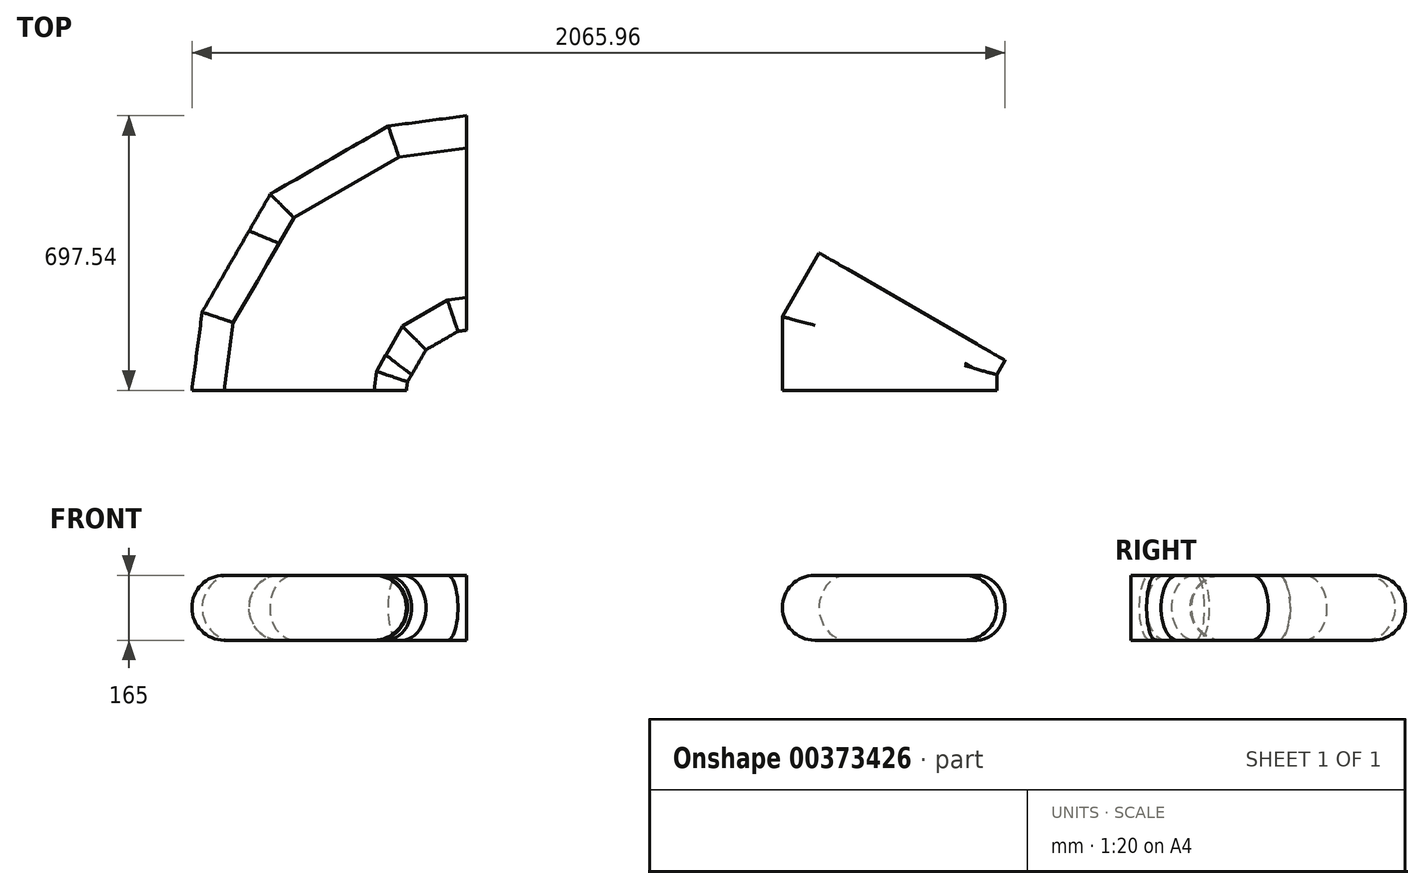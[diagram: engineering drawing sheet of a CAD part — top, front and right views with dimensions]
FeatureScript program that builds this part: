
annotation { "Feature Type Name" : "Feature", "Feature Type Description" : "" }
export const myFeature = defineFeature(function(context is Context, id is Id, definition is map)
    precondition{}
    {
        {
            var Q0;
            Q0=qCreatedBy(makeId("Top.planeOp"),FACE);
            var sketch = newSketch(context, id + "F0", { "sketchPlane" : qUnion([Q0])});
            skLineSegment(sketch, "E0.bottom", {"start": v(272.5, -57) * mm, "end": v(-272.5, -57) * mm});
            skLineSegment(sketch, "E0.top", {"start": v(272.5, 57) * mm, "end": v(-272.5, 57) * mm});
            skLineSegment(sketch, "E0.left", {"start": v(272.5, -57) * mm, "end": v(272.5, 57) * mm});
            skLineSegment(sketch, "E0.right", {"start": v(-272.5, -57) * mm, "end": v(-272.5, 57) * mm});
            skPoint(sketch, "E0.middle", {"position": v(0, 0) * mm});
            skLineSegment(sketch, "E1", {"start": v(0, -57) * mm, "end": v(425, -57) * mm, "construction": true});
            skCircle(sketch, "E2", {"center": v(425, -57) * mm, "radius": 425 * mm, "construction": true});
            skLineSegment(sketch, "E3", {"start": v(425, -57) * mm, "end": v(0, 57) * mm, "construction": true});
            skLineSegment(sketch, "E4", {"start": v(-272.5, 57) * mm, "end": v(-272.5, 312.2) * mm, "construction": true});
            skLineSegment(sketch, "E5", {"start": v(0, 57) * mm, "end": v(-272.5, 130.1) * mm, "construction": true});
            skLineSegment(sketch, "E6", {"start": v(29.53, 167.1) * mm, "end": v(292.73, 96.5) * mm, "construction": true});
            skLineSegment(sketch, "E7", {"start": v(29.53, 167.1) * mm, "end": v(-233.66, 237.7) * mm, "construction": true});
            skLineSegment(sketch, "E8", {"start": v(-272.5, 57) * mm, "end": v(-272.5, 130.1) * mm});
            skLineSegment(sketch, "E9", {"start": v(-272.5, 130.1) * mm, "end": v(-233.66, 237.7) * mm});
            skLineSegment(sketch, "E10", {"start": v(-233.66, 237.7) * mm, "end": v(292.73, 96.5) * mm});
            skLineSegment(sketch, "E11", {"start": v(292.73, 96.5) * mm, "end": v(272.5, -16.1) * mm});
            skLineSegment(sketch, "E12", {"start": v(29.53, 167.1) * mm, "end": v(0, 57) * mm});
            skLineSegment(sketch, "E13", {"start": v(0, 57) * mm, "end": v(0, -57) * mm});
            skSolve(sketch);
        }
        {
            var Q0;
            Q0=qCreatedBy(makeId("Front.planeOp"),FACE);
            var sketch = newSketch(context, id + "F1", { "sketchPlane" : qUnion([Q0])});
            skLineSegment(sketch, "E14.bottom", {"start": v(190, -82.5) * mm, "end": v(-190, -82.5) * mm});
            skLineSegment(sketch, "E14.top", {"start": v(190, 82.5) * mm, "end": v(-190, 82.5) * mm});
            skLineSegment(sketch, "E14.left", {"start": v(190, -82.5) * mm, "end": v(190, 82.5) * mm});
            skLineSegment(sketch, "E14.right", {"start": v(-190, -82.5) * mm, "end": v(-190, 82.5) * mm});
            skPoint(sketch, "E14.middle", {"position": v(0, 0) * mm});
            skArc(sketch, "E15", {"start": v(-190, 82.5) * mm, "mid": v(-272.5, 0) * mm, "end": v(-190, -82.5) * mm});
            skArc(sketch, "E16", {"start": v(190, -82.5) * mm, "mid": v(272.5, 0) * mm, "end": v(190, 82.5) * mm});
            skSolve(sketch);
        }
        {
            var Q0;
            Q0=sQuery(id+"F0.wireOp",EDGE,"E10");
            cPlane(context, id + "F2", {"entities" : qUnion([Q0]), "cplaneType" : CPlaneType.LINE_ANGLE, "offset" : 25 * mm, "angle" : 0 * degree, "width" : 150 * mm, "height" : 150 * mm});
        }
        {
            var Q0;
            Q0=qCreatedBy(id+"F2.planeOp",FACE);
            var sketch = newSketch(context, id + "F3", { "sketchPlane" : qUnion([Q0])});
            skPoint(sketch, "E17.middle", {"position": v(0, 0) * mm});
            skLineSegment(sketch, "E18.bottom", {"start": v(204.8, -82.5) * mm, "end": v(-175.2, -82.5) * mm});
            skLineSegment(sketch, "E18.top", {"start": v(204.8, 82.5) * mm, "end": v(-175.2, 82.5) * mm});
            skLineSegment(sketch, "E18.left", {"start": v(204.8, -82.5) * mm, "end": v(204.8, 82.5) * mm});
            skLineSegment(sketch, "E18.right", {"start": v(-175.2, -82.5) * mm, "end": v(-175.2, 82.5) * mm});
            skPoint(sketch, "E18.middle", {"position": v(14.8, 0) * mm});
            skArc(sketch, "E19", {"start": v(-175.2, 82.5) * mm, "mid": v(-257.7, 0) * mm, "end": v(-175.2, -82.5) * mm});
            skArc(sketch, "E20", {"start": v(204.8, -82.5) * mm, "mid": v(287.3, 0) * mm, "end": v(204.8, 82.5) * mm});
            skSolve(sketch);
        }
        {
            var Q0;
            Q0=makeQuery(id+"F3.imprint","IMPRINT",FACE,{"disambiguationData":[TD([[makeQuery(id+"F3.imprint","IMPRINT",EDGE,{"derivedFrom":sQuery(id+"F3.wireOp",EDGE,"E18.bottom")}),-1.0]])]});
            var Q1;
            Q1=makeQuery(id+"F3.imprint","IMPRINT",FACE,{"disambiguationData":[TD([[makeQuery(id+"F3.imprint","IMPRINT",EDGE,{"derivedFrom":sQuery(id+"F3.wireOp",EDGE,"E18.right")}),1.0]])]});
            var Q2;
            Q2=makeQuery(id+"F3.imprint","IMPRINT",FACE,{"disambiguationData":[TD([[makeQuery(id+"F3.imprint","IMPRINT",EDGE,{"derivedFrom":sQuery(id+"F3.wireOp",EDGE,"E18.left")}),-1.0]])]});
            var Q3;
            Q3=sQuery(id+"F0.wireOp",EDGE,"E12");
            var Q4;
            Q4=sQuery(id+"F0.wireOp",EDGE,"E13");
            sweep(context, id + "F4", {"profiles" : qUnion([Q0, Q1, Q2]), "path" : qUnion([Q3, Q4])});
        }
        {
            var Q0;
            Q0=qCreatedBy(makeId("Top.planeOp"),FACE);
            var sketch = newSketch(context, id + "F5", { "sketchPlane" : qUnion([Q0])});
            skLineSegment(sketch, "E21", {"start": v(0, 0) * mm, "end": v(1000, 0) * mm, "construction": true});
            skLineSegment(sketch, "E22", {"start": v(1000, 0) * mm, "end": v(1000, 500) * mm, "construction": true});
            skLineSegment(sketch, "E23", {"start": v(1000, 0) * mm, "end": v(1000, -500) * mm, "construction": true});
            skLineSegment(sketch, "E24", {"start": v(1000, 0) * mm, "end": v(1425, 0) * mm, "construction": true});
            skCircle(sketch, "E25", {"center": v(1425, 0) * mm, "radius": 425 * mm, "construction": true});
            skLineSegment(sketch, "E26", {"start": v(1014.48, 110) * mm, "end": v(1425, 0) * mm, "construction": true});
            skLineSegment(sketch, "E27", {"start": v(1124.48, 300.52) * mm, "end": v(1425, 0) * mm, "construction": true});
            skLineSegment(sketch, "E28", {"start": v(1315, 410.52) * mm, "end": v(1425, 0) * mm, "construction": true});
            skLineSegment(sketch, "E29", {"start": v(1425, 425) * mm, "end": v(1425, 0) * mm, "construction": true});
            skLineSegment(sketch, "E30", {"start": v(1000, 0) * mm, "end": v(1014.48, 110) * mm});
            skLineSegment(sketch, "E31", {"start": v(1124.48, 300.52) * mm, "end": v(1315, 410.52) * mm});
            skLineSegment(sketch, "E32", {"start": v(1069.48, 205.26) * mm, "end": v(1124.48, 300.52) * mm});
            skLineSegment(sketch, "E33", {"start": v(1315, 410.52) * mm, "end": v(1425, 425) * mm});
            skPoint(sketch, "E34", {"position": v(1069.48, 205.26) * mm});
            skLineSegment(sketch, "E35", {"start": v(1014.48, 110) * mm, "end": v(1069.48, 205.26) * mm});
            skSolve(sketch);
        }
        {
            var Q0;
            Q0=sQuery(id+"F5.wireOp",EDGE,"E29");
            cPlane(context, id + "F6", {"entities" : qUnion([Q0]), "cplaneType" : CPlaneType.LINE_ANGLE, "offset" : 25 * mm, "angle" : 90 * degree, "width" : 150 * mm, "height" : 150 * mm});
        }
        {
            var Q0;
            Q0=qCreatedBy(id+"F6.planeOp",FACE);
            var sketch = newSketch(context, id + "F7", { "sketchPlane" : qUnion([Q0])});
            skLineSegment(sketch, "E36.bottom", {"start": v(615.04, -82.5) * mm, "end": v(235.04, -82.5) * mm});
            skLineSegment(sketch, "E36.top", {"start": v(615.04, 82.5) * mm, "end": v(235.04, 82.5) * mm});
            skPoint(sketch, "E36.middle", {"position": v(425.04, 0) * mm});
            skArc(sketch, "E37", {"start": v(235.04, 82.5) * mm, "mid": v(152.54, 0) * mm, "end": v(235.04, -82.5) * mm});
            skArc(sketch, "E38", {"start": v(615.04, -82.5) * mm, "mid": v(697.54, 0) * mm, "end": v(615.04, 82.5) * mm});
            skSolve(sketch);
        }
        {
            var Q0;
            Q0=makeQuery(id+"F1.imprint","IMPRINT",FACE,{"disambiguationData":[TD([[makeQuery(id+"F1.imprint","IMPRINT",EDGE,{"derivedFrom":sQuery(id+"F1.wireOp",EDGE,"E14.bottom")}),-1.0]])]});
            var sketch = newSketch(context, id + "F8", { "sketchPlane" : qUnion([Q0])});
            skLineSegment(sketch, "E39.bottom", {"start": v(1189.85, -82.5) * mm, "end": v(809.85, -82.5) * mm});
            skLineSegment(sketch, "E39.top", {"start": v(1189.85, 82.5) * mm, "end": v(809.85, 82.5) * mm});
            skPoint(sketch, "E39.middle", {"position": v(999.85, 0) * mm});
            skArc(sketch, "E40", {"start": v(809.85, 82.5) * mm, "mid": v(727.35, 0) * mm, "end": v(809.85, -82.5) * mm});
            skArc(sketch, "E41", {"start": v(1189.85, -82.5) * mm, "mid": v(1272.35, 0) * mm, "end": v(1189.85, 82.5) * mm});
            skSolve(sketch);
        }
        {
            var Q0;
            Q0=makeQuery(id+"F7.imprint","IMPRINT",FACE,{"disambiguationData":[TD([[makeQuery(id+"F7.imprint","IMPRINT",EDGE,{"derivedFrom":sQuery(id+"F7.wireOp",EDGE,"E36.bottom")}),-1.0]])]});
            var Q1;
            Q1=sQuery(id+"F5.wireOp",EDGE,"E33");
            var Q2;
            Q2=sQuery(id+"F5.wireOp",EDGE,"E31");
            var Q3;
            Q3=sQuery(id+"F5.wireOp",EDGE,"E32");
            sweep(context, id + "F9", {"profiles" : qUnion([Q0]), "path" : qUnion([Q1, Q2, Q3])});
        }
        {
            var Q0;
            Q0=makeQuery(id+"F8.imprint","IMPRINT",FACE,{"disambiguationData":[TD([[makeQuery(id+"F8.imprint","IMPRINT",EDGE,{"derivedFrom":sQuery(id+"F8.wireOp",EDGE,"E39.bottom")}),-1.0]])]});
            var Q1;
            Q1=sQuery(id+"F5.wireOp",EDGE,"E30");
            var Q2;
            Q2=sQuery(id+"F5.wireOp",EDGE,"E35");
            var Q3;
            Q3=sQuery(id+"F5.wireOp",EDGE,"E32");
            sweep(context, id + "F10", {"operationType" : NewBodyOperationType.ADD, "profiles" : qUnion([Q0]), "path" : qUnion([Q1, Q2, Q3])});
        }
        {
            var Q0;
            Q0=qCreatedBy(makeId("Top.planeOp"),FACE);
            var sketch = newSketch(context, id + "F11", { "sketchPlane" : qUnion([Q0])});
            skLineSegment(sketch, "E42", {"start": v(0, 0) * mm, "end": v(2500, 0) * mm, "construction": true});
            skLineSegment(sketch, "E43", {"start": v(2500, 0) * mm, "end": v(2925, 0) * mm, "construction": true});
            skCircle(sketch, "E44", {"center": v(2925, 0) * mm, "radius": 425 * mm, "construction": true});
            skLineSegment(sketch, "E45", {"start": v(2556.94, 212.5) * mm, "end": v(2925, 0) * mm, "construction": true});
            skLineSegment(sketch, "E46", {"start": v(2500, 0) * mm, "end": v(2500, 114) * mm, "construction": true});
            skLineSegment(sketch, "E47", {"start": v(2556.94, 212.5) * mm, "end": v(2792.93, 76.25) * mm, "construction": true});
            skLineSegment(sketch, "E48", {"start": v(2556.94, 212.5) * mm, "end": v(2321.02, 348.88) * mm, "construction": true});
            skLineSegment(sketch, "E49", {"start": v(2500, 114) * mm, "end": v(2556.94, 212.5) * mm});
            skLineSegment(sketch, "E50", {"start": v(2500, 0) * mm, "end": v(2500, 114) * mm});
            skLineSegment(sketch, "E51", {"start": v(2556.94, 212.5) * mm, "end": v(2528.47, 163.25) * mm});
            skSolve(sketch);
        }
        {
            var Q0;
            Q0=sQuery(id+"F11.wireOp",EDGE,"E43");
            cPlane(context, id + "F12", {"entities" : qUnion([Q0]), "cplaneType" : CPlaneType.LINE_ANGLE, "offset" : 25 * mm, "angle" : 180 * degree, "width" : 150 * mm, "height" : 150 * mm});
        }
        {
            var Q0;
            Q0=qCreatedBy(id+"F12.planeOp",FACE);
            var sketch = newSketch(context, id + "F13", { "sketchPlane" : qUnion([Q0])});
            skLineSegment(sketch, "E52.bottom", {"start": v(2689.9, -82.5) * mm, "end": v(2309.9, -82.5) * mm});
            skLineSegment(sketch, "E52.top", {"start": v(2689.9, 82.5) * mm, "end": v(2309.9, 82.5) * mm});
            skPoint(sketch, "E52.middle", {"position": v(2499.9, 0) * mm});
            skArc(sketch, "E53", {"start": v(2309.9, 82.5) * mm, "mid": v(2227.4, 0) * mm, "end": v(2309.9, -82.5) * mm});
            skArc(sketch, "E54", {"start": v(2689.9, -82.5) * mm, "mid": v(2772.4, 0) * mm, "end": v(2689.9, 82.5) * mm});
            skSolve(sketch);
        }
        {
            var Q0;
            Q0=sQuery(id+"F11.wireOp",EDGE,"E48");
            cPlane(context, id + "F14", {"entities" : qUnion([Q0]), "cplaneType" : CPlaneType.LINE_ANGLE, "offset" : 25 * mm, "angle" : 180 * degree, "width" : 150 * mm, "height" : 150 * mm});
        }
        {
            var Q0;
            Q0=qCreatedBy(id+"F14.planeOp",FACE);
            var sketch = newSketch(context, id + "F15", { "sketchPlane" : qUnion([Q0])});
            skLineSegment(sketch, "E55.bottom", {"start": v(-1917.87, -82.5) * mm, "end": v(-2297.87, -82.5) * mm});
            skLineSegment(sketch, "E55.top", {"start": v(-1917.87, 82.5) * mm, "end": v(-2297.87, 82.5) * mm});
            skPoint(sketch, "E55.middle", {"position": v(-2107.87, 0) * mm});
            skArc(sketch, "E56", {"start": v(-2297.87, 82.5) * mm, "mid": v(-2380.37, 0) * mm, "end": v(-2297.87, -82.5) * mm});
            skArc(sketch, "E57", {"start": v(-1917.87, -82.5) * mm, "mid": v(-1835.37, 0) * mm, "end": v(-1917.87, 82.5) * mm});
            skSolve(sketch);
        }
        {
            var Q0;
            Q0=makeQuery(id+"F15.imprint","IMPRINT",FACE,{"disambiguationData":[TD([[makeQuery(id+"F15.imprint","IMPRINT",EDGE,{"derivedFrom":sQuery(id+"F15.wireOp",EDGE,"E55.bottom")}),-1.0]])]});
            var Q1;
            Q1=sQuery(id+"F11.wireOp",EDGE,"E51");
            sweep(context, id + "F16", {"profiles" : qUnion([Q0]), "path" : qUnion([Q1])});
        }
        {
            var Q0;
            Q0=makeQuery(id+"F13.imprint","IMPRINT",FACE,{"disambiguationData":[TD([[makeQuery(id+"F13.imprint","IMPRINT",EDGE,{"derivedFrom":sQuery(id+"F13.wireOp",EDGE,"E52.bottom")}),-1.0]])]});
            var Q1;
            Q1=sQuery(id+"F11.wireOp",EDGE,"E50");
            var Q2;
            Q2=sQuery(id+"F11.wireOp",EDGE,"E49");
            sweep(context, id + "F17", {"operationType" : NewBodyOperationType.ADD, "profiles" : qUnion([Q0]), "path" : qUnion([Q1, Q2])});
        }
        {
            var Q0;
            Q0=makeQuery(id+"F4.opSweep","SWEPT_BODY",BODY,{"disambiguationData":[OSD([sQuery(id+"F0.wireOp",EDGE,"E13"),sQuery(id+"F3.wireOp",EDGE,"E18.bottom"),sQuery(id+"F3.wireOp",EDGE,"E18.top"),sQuery(id+"F3.wireOp",EDGE,"E19"),sQuery(id+"F3.wireOp",EDGE,"E20")])]});
            deleteBodies(context, id + "F18", {"entities" : qUnion([Q0])});
        }
        {
            var Q0;
            Q0=makeQuery(id+"F9.opSweep","SWEPT_BODY",BODY,{"disambiguationData":[OSD([sQuery(id+"F5.wireOp",EDGE,"E32"),sQuery(id+"F7.wireOp",EDGE,"E36.bottom"),sQuery(id+"F7.wireOp",EDGE,"E36.top"),sQuery(id+"F7.wireOp",EDGE,"E37"),sQuery(id+"F7.wireOp",EDGE,"E38")])]});
            transform(context, id + "F19", {"entities" : qUnion([Q0]), "transformType" : TransformType.COPY});
        }
    });
